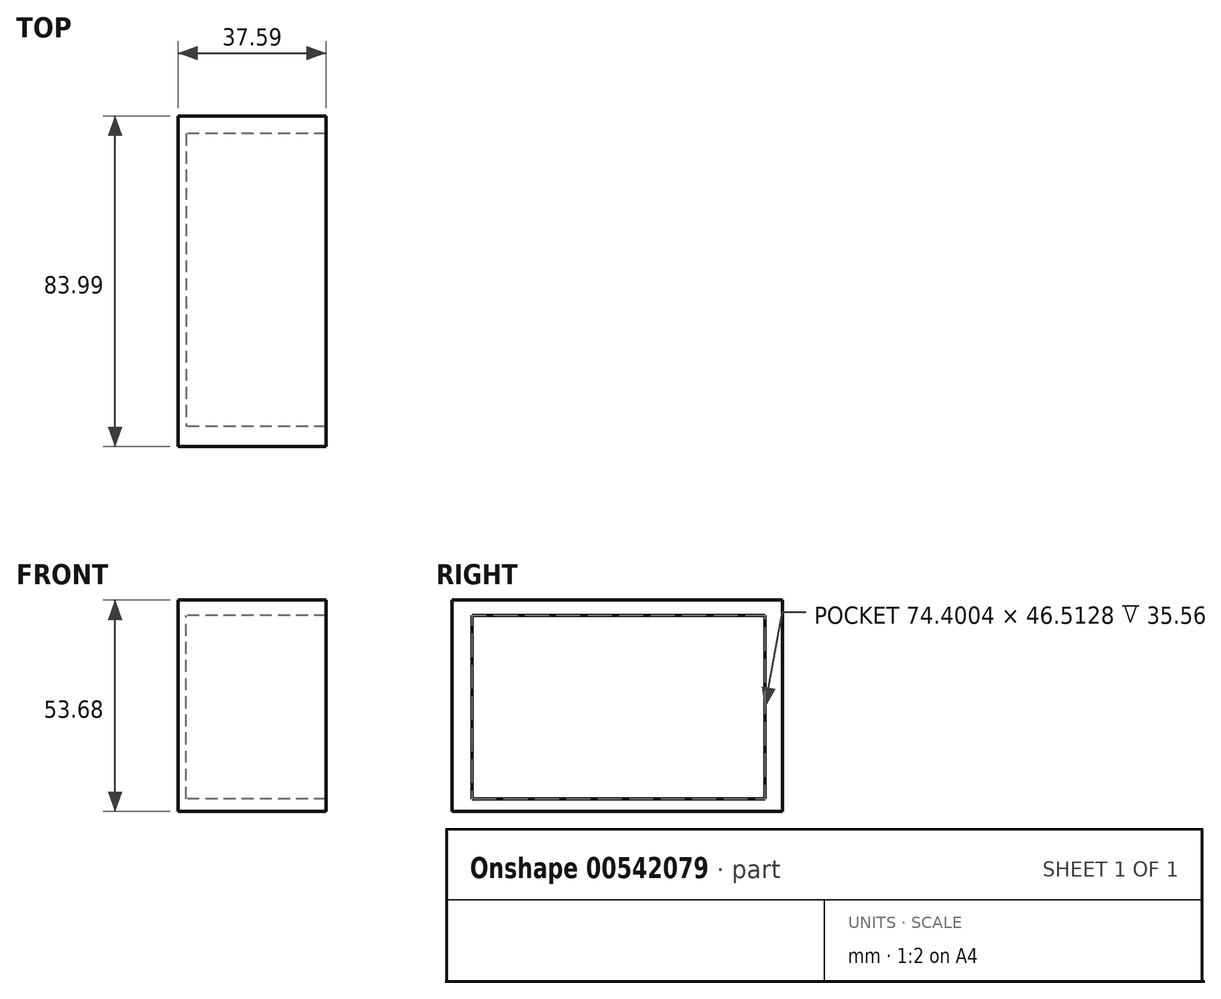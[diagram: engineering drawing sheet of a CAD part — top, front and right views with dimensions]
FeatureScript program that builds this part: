
annotation { "Feature Type Name" : "Feature", "Feature Type Description" : "" }
export const myFeature = defineFeature(function(context is Context, id is Id, definition is map)
    precondition{}
    {
        {
            var Q0;
            Q0=qCreatedBy(makeId("Right.planeOp"),FACE);
            var sketch = newSketch(context, id + "F0", { "sketchPlane" : qUnion([Q0])});
            skLineSegment(sketch, "E0.bottom", {"start": v(-38.5, -23.77) * mm, "end": v(45.48, -23.77) * mm});
            skLineSegment(sketch, "E0.top", {"start": v(-38.5, 29.91) * mm, "end": v(45.48, 29.91) * mm});
            skLineSegment(sketch, "E0.left", {"start": v(-38.5, -23.77) * mm, "end": v(-38.5, 29.91) * mm});
            skLineSegment(sketch, "E0.right", {"start": v(45.48, -23.77) * mm, "end": v(45.48, 29.91) * mm});
            skSolve(sketch);
        }
        {
            var Q0;
            Q0=makeQuery(id+"F0.imprint","IMPRINT",FACE,{"disambiguationData":[TD([[makeQuery(id+"F0.imprint","IMPRINT",EDGE,{"derivedFrom":sQuery(id+"F0.wireOp",EDGE,"E0.bottom")}),1.0]])]});
            extrude(context, id + "F1", {"entities" : qUnion([Q0]), "depth" : 2.03 * mm, "offsetDistance" : 25.4 * mm});
        }
        {
            var Q0;
            Q0=makeQuery(id+"F1.opExtrude","CAP_FACE",FACE,{"disambiguationData":[OSD([sQuery(id+"F0.wireOp",EDGE,"E0.bottom"),sQuery(id+"F0.wireOp",EDGE,"E0.top"),sQuery(id+"F0.wireOp",EDGE,"E0.left"),sQuery(id+"F0.wireOp",EDGE,"E0.right")])],"isStart":false});
            var sketch = newSketch(context, id + "F2", { "sketchPlane" : qUnion([Q0])});
            skLineSegment(sketch, "E1.bottom", {"start": v(45.48, -23.77) * mm, "end": v(-33.37, -23.77) * mm});
            skLineSegment(sketch, "E1.top", {"start": v(45.48, -20.54) * mm, "end": v(-33.37, -20.54) * mm});
            skLineSegment(sketch, "E1.left", {"start": v(45.48, -23.77) * mm, "end": v(45.48, -20.54) * mm});
            skLineSegment(sketch, "E1.right", {"start": v(-33.37, -23.77) * mm, "end": v(-33.37, -20.54) * mm});
            skSolve(sketch);
        }
        {
            var Q0;
            Q0 = qSketchRegion(id + "F2", true);
            extrude(context, id + "F3", {"entities" : qUnion([Q0]), "operationType" : NewBodyOperationType.ADD, "depth" : 35.56 * mm, "offsetDistance" : 25.4 * mm});
        }
        {
            var Q0;
            Q0=makeQuery(id+"F1.opExtrude","CAP_FACE",FACE,{"disambiguationData":[OSD([sQuery(id+"F0.wireOp",EDGE,"E0.bottom"),sQuery(id+"F0.wireOp",EDGE,"E0.top"),sQuery(id+"F0.wireOp",EDGE,"E0.left"),sQuery(id+"F0.wireOp",EDGE,"E0.right")])],"isStart":false});
            var sketch = newSketch(context, id + "F4", { "sketchPlane" : qUnion([Q0])});
            skLineSegment(sketch, "E2.bottom", {"start": v(-33.37, -23.77) * mm, "end": v(-38.5, -23.77) * mm});
            skLineSegment(sketch, "E2.top", {"start": v(-33.37, 29.91) * mm, "end": v(-38.5, 29.91) * mm});
            skLineSegment(sketch, "E2.left", {"start": v(-33.37, -23.77) * mm, "end": v(-33.37, 29.91) * mm});
            skLineSegment(sketch, "E2.right", {"start": v(-38.5, -23.77) * mm, "end": v(-38.5, 29.91) * mm});
            skSolve(sketch);
        }
        {
            var Q0;
            Q0 = qSketchRegion(id + "F4", true);
            extrude(context, id + "F5", {"entities" : qUnion([Q0]), "operationType" : NewBodyOperationType.ADD, "depth" : 35.56 * mm, "offsetDistance" : 25.4 * mm});
        }
        {
            var Q0;
            Q0=makeQuery(id+"F1.opExtrude","CAP_FACE",FACE,{"disambiguationData":[OSD([sQuery(id+"F0.wireOp",EDGE,"E0.bottom"),sQuery(id+"F0.wireOp",EDGE,"E0.top"),sQuery(id+"F0.wireOp",EDGE,"E0.left"),sQuery(id+"F0.wireOp",EDGE,"E0.right")])],"isStart":false});
            var sketch = newSketch(context, id + "F6", { "sketchPlane" : qUnion([Q0])});
            skLineSegment(sketch, "E3.bottom", {"start": v(-36.57, 29.91) * mm, "end": v(45.48, 29.91) * mm});
            skLineSegment(sketch, "E3.top", {"start": v(-36.57, 25.98) * mm, "end": v(45.48, 25.98) * mm});
            skLineSegment(sketch, "E3.left", {"start": v(-36.57, 29.91) * mm, "end": v(-36.57, 25.98) * mm});
            skLineSegment(sketch, "E3.right", {"start": v(45.48, 29.91) * mm, "end": v(45.48, 25.98) * mm});
            skSolve(sketch);
        }
        {
            var Q0;
            Q0 = qSketchRegion(id + "F6", true);
            extrude(context, id + "F7", {"entities" : qUnion([Q0]), "operationType" : NewBodyOperationType.ADD, "depth" : 35.56 * mm, "offsetDistance" : 25.4 * mm});
        }
        {
            var Q0;
            Q0=makeQuery(id+"F1.opExtrude","CAP_FACE",FACE,{"disambiguationData":[OSD([sQuery(id+"F0.wireOp",EDGE,"E0.bottom"),sQuery(id+"F0.wireOp",EDGE,"E0.top"),sQuery(id+"F0.wireOp",EDGE,"E0.left"),sQuery(id+"F0.wireOp",EDGE,"E0.right")])],"isStart":false});
            var sketch = newSketch(context, id + "F8", { "sketchPlane" : qUnion([Q0])});
            skLineSegment(sketch, "E4.bottom", {"start": v(45.48, -20.54) * mm, "end": v(41.03, -20.54) * mm});
            skLineSegment(sketch, "E4.top", {"start": v(45.48, 28.58) * mm, "end": v(41.03, 28.58) * mm});
            skLineSegment(sketch, "E4.left", {"start": v(45.48, -20.54) * mm, "end": v(45.48, 28.58) * mm});
            skLineSegment(sketch, "E4.right", {"start": v(41.03, -20.54) * mm, "end": v(41.03, 28.58) * mm});
            skSolve(sketch);
        }
        {
            var Q0;
            Q0 = qSketchRegion(id + "F8", true);
            extrude(context, id + "F9", {"entities" : qUnion([Q0]), "operationType" : NewBodyOperationType.ADD, "depth" : 35.56 * mm, "offsetDistance" : 25.4 * mm});
        }
    });
